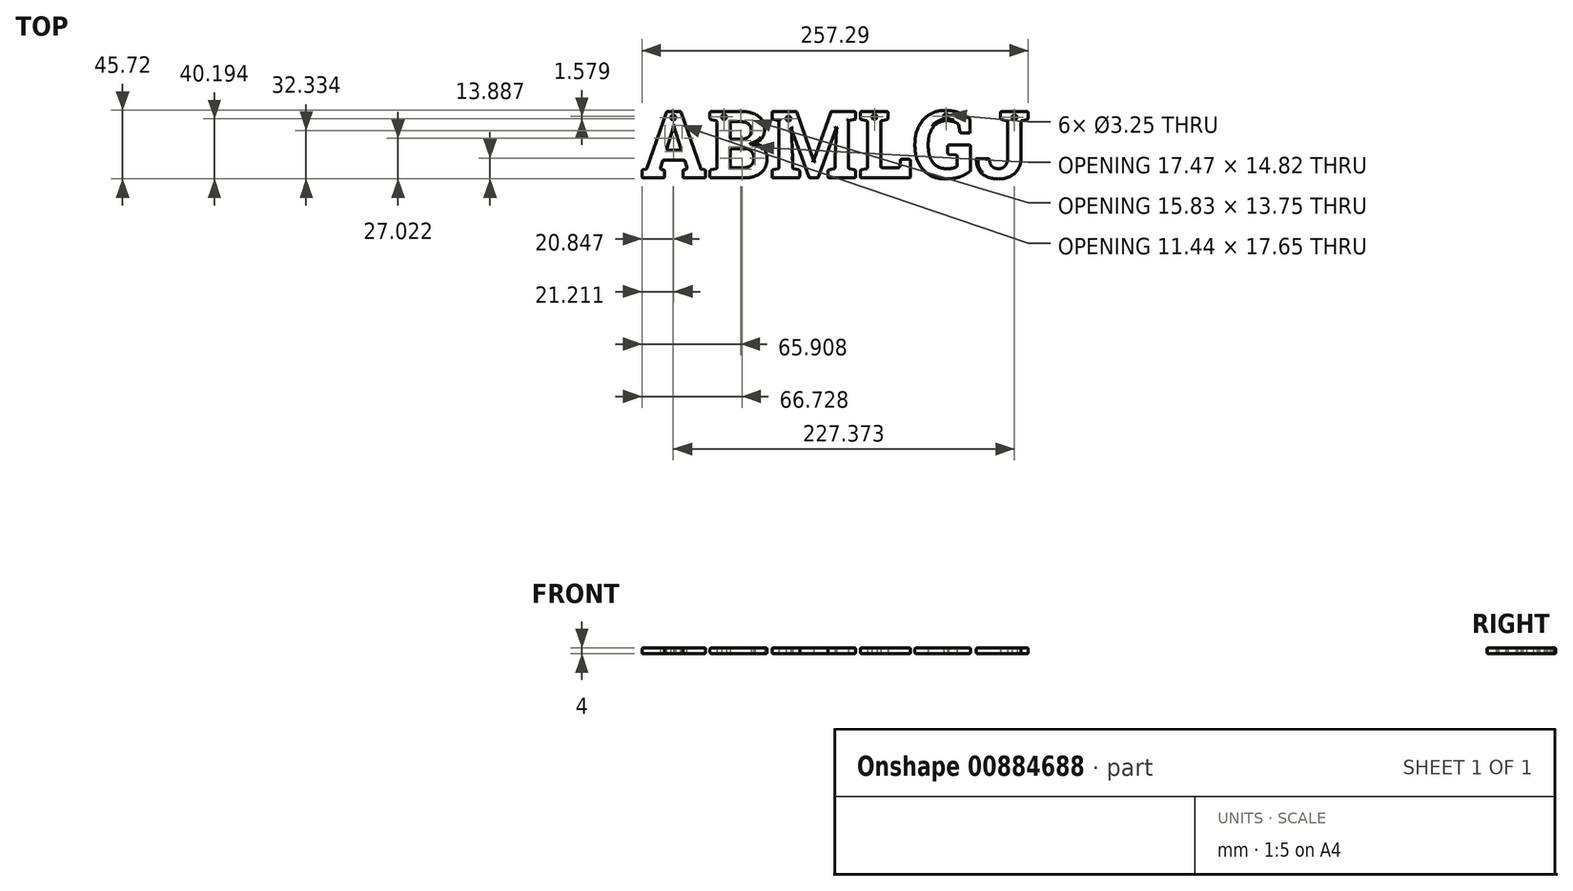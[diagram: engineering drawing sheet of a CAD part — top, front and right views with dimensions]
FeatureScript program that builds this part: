
annotation { "Feature Type Name" : "Feature", "Feature Type Description" : "" }
export const myFeature = defineFeature(function(context is Context, id is Id, definition is map)
    precondition{}
    {
        {
            var Q0;
            Q0=qCreatedBy(makeId("Top.planeOp"),FACE);
            var sketch = newSketch(context, id + "F0", { "sketchPlane" : qUnion([Q0])});
            skText(sketch, "E0", { "text": "ABMLGJ", "fontName": "RobotoSlab-Bold.ttf"});
            skCircle(sketch, "E1", {"center": v(-18.26, 12.84) * mm, "radius": 1.63 * mm});
            skCircle(sketch, "E2", {"center": v(15.58, 13.2) * mm, "radius": 1.63 * mm});
            skCircle(sketch, "E3", {"center": v(58.54, 12.08) * mm, "radius": 1.63 * mm});
            skCircle(sketch, "E4", {"center": v(115.8, 13.22) * mm, "radius": 1.63 * mm});
            skCircle(sketch, "E5", {"center": v(163.46, 13.66) * mm, "radius": 1.63 * mm});
            skCircle(sketch, "E6", {"center": v(209.1, 12.89) * mm, "radius": 1.63 * mm});
            const initialGuessF0  = {"E0": [-0.04036, -0.02747, 1, 0, 0.045]};
            skSetInitialGuess(sketch, initialGuessF0);
            skSolve(sketch);
        }
        {
            var Q0;
            Q0 = qSketchRegion(id + "F0", true);
            extrude(context, id + "F1", {"entities" : qUnion([Q0]), "depth" : 4 * mm, "offsetDistance" : 25 * mm});
        }
        {
            var Q0;
            Q0=makeQuery(id+"F1.opExtrude","CAP_FACE",FACE,{"disambiguationData":[OSD([sQuery(id+"F0.wireOp",EDGE,"E0.sketch_text.stroke-20"),sQuery(id+"F0.wireOp",EDGE,"E0.sketch_text.stroke-21"),sQuery(id+"F0.wireOp",EDGE,"E0.sketch_text.stroke-22"),sQuery(id+"F0.wireOp",EDGE,"E0.sketch_text.stroke-23"),sQuery(id+"F0.wireOp",EDGE,"E0.sketch_text.stroke-24"),sQuery(id+"F0.wireOp",EDGE,"E0.sketch_text.stroke-25"),sQuery(id+"F0.wireOp",EDGE,"E0.sketch_text.stroke-26"),sQuery(id+"F0.wireOp",EDGE,"E0.sketch_text.stroke-27"),sQuery(id+"F0.wireOp",EDGE,"E0.sketch_text.stroke-28"),sQuery(id+"F0.wireOp",EDGE,"E0.sketch_text.stroke-29"),sQuery(id+"F0.wireOp",EDGE,"E0.sketch_text.stroke-30"),sQuery(id+"F0.wireOp",EDGE,"E0.sketch_text.stroke-31"),sQuery(id+"F0.wireOp",EDGE,"E0.sketch_text.stroke-32"),sQuery(id+"F0.wireOp",EDGE,"E0.sketch_text.stroke-33"),sQuery(id+"F0.wireOp",EDGE,"E0.sketch_text.stroke-34"),sQuery(id+"F0.wireOp",EDGE,"E0.sketch_text.stroke-35"),sQuery(id+"F0.wireOp",EDGE,"E0.sketch_text.stroke-36"),sQuery(id+"F0.wireOp",EDGE,"E0.sketch_text.stroke-37"),sQuery(id+"F0.wireOp",EDGE,"E0.sketch_text.stroke-38"),sQuery(id+"F0.wireOp",EDGE,"E0.sketch_text.stroke-39"),sQuery(id+"F0.wireOp",EDGE,"E0.sketch_text.stroke-40"),sQuery(id+"F0.wireOp",EDGE,"E0.sketch_text.stroke-41"),sQuery(id+"F0.wireOp",EDGE,"E0.sketch_text.stroke-42"),sQuery(id+"F0.wireOp",EDGE,"E0.sketch_text.stroke-43"),sQuery(id+"F0.wireOp",EDGE,"E0.sketch_text.stroke-44"),sQuery(id+"F0.wireOp",EDGE,"E0.sketch_text.stroke-45"),sQuery(id+"F0.wireOp",EDGE,"E0.sketch_text.stroke-46"),sQuery(id+"F0.wireOp",EDGE,"E0.sketch_text.stroke-47"),sQuery(id+"F0.wireOp",EDGE,"E0.sketch_text.stroke-48"),sQuery(id+"F0.wireOp",EDGE,"E0.sketch_text.stroke-49"),sQuery(id+"F0.wireOp",EDGE,"E2")])],"isStart":false});
            var Q1;
            Q1=makeQuery(id+"F1.opExtrude","CAP_FACE",FACE,{"disambiguationData":[OSD([sQuery(id+"F0.wireOp",EDGE,"E0.sketch_text.stroke-50"),sQuery(id+"F0.wireOp",EDGE,"E0.sketch_text.stroke-51"),sQuery(id+"F0.wireOp",EDGE,"E0.sketch_text.stroke-52"),sQuery(id+"F0.wireOp",EDGE,"E0.sketch_text.stroke-53"),sQuery(id+"F0.wireOp",EDGE,"E0.sketch_text.stroke-54"),sQuery(id+"F0.wireOp",EDGE,"E0.sketch_text.stroke-55"),sQuery(id+"F0.wireOp",EDGE,"E0.sketch_text.stroke-56"),sQuery(id+"F0.wireOp",EDGE,"E0.sketch_text.stroke-57"),sQuery(id+"F0.wireOp",EDGE,"E0.sketch_text.stroke-58"),sQuery(id+"F0.wireOp",EDGE,"E0.sketch_text.stroke-59"),sQuery(id+"F0.wireOp",EDGE,"E0.sketch_text.stroke-60"),sQuery(id+"F0.wireOp",EDGE,"E0.sketch_text.stroke-61"),sQuery(id+"F0.wireOp",EDGE,"E0.sketch_text.stroke-62"),sQuery(id+"F0.wireOp",EDGE,"E0.sketch_text.stroke-63"),sQuery(id+"F0.wireOp",EDGE,"E0.sketch_text.stroke-64"),sQuery(id+"F0.wireOp",EDGE,"E0.sketch_text.stroke-65"),sQuery(id+"F0.wireOp",EDGE,"E0.sketch_text.stroke-66"),sQuery(id+"F0.wireOp",EDGE,"E0.sketch_text.stroke-67"),sQuery(id+"F0.wireOp",EDGE,"E0.sketch_text.stroke-68"),sQuery(id+"F0.wireOp",EDGE,"E0.sketch_text.stroke-69"),sQuery(id+"F0.wireOp",EDGE,"E0.sketch_text.stroke-70"),sQuery(id+"F0.wireOp",EDGE,"E0.sketch_text.stroke-71"),sQuery(id+"F0.wireOp",EDGE,"E0.sketch_text.stroke-72"),sQuery(id+"F0.wireOp",EDGE,"E0.sketch_text.stroke-73"),sQuery(id+"F0.wireOp",EDGE,"E0.sketch_text.stroke-74"),sQuery(id+"F0.wireOp",EDGE,"E0.sketch_text.stroke-75"),sQuery(id+"F0.wireOp",EDGE,"E0.sketch_text.stroke-76"),sQuery(id+"F0.wireOp",EDGE,"E0.sketch_text.stroke-77"),sQuery(id+"F0.wireOp",EDGE,"E0.sketch_text.stroke-78"),sQuery(id+"F0.wireOp",EDGE,"E0.sketch_text.stroke-79"),sQuery(id+"F0.wireOp",EDGE,"E0.sketch_text.stroke-80"),sQuery(id+"F0.wireOp",EDGE,"E3")])],"isStart":false});
            var Q2;
            Q2=makeQuery(id+"F1.opExtrude","CAP_FACE",FACE,{"disambiguationData":[OSD([sQuery(id+"F0.wireOp",EDGE,"E0.sketch_text.stroke-81"),sQuery(id+"F0.wireOp",EDGE,"E0.sketch_text.stroke-82"),sQuery(id+"F0.wireOp",EDGE,"E0.sketch_text.stroke-83"),sQuery(id+"F0.wireOp",EDGE,"E0.sketch_text.stroke-84"),sQuery(id+"F0.wireOp",EDGE,"E0.sketch_text.stroke-85"),sQuery(id+"F0.wireOp",EDGE,"E0.sketch_text.stroke-86"),sQuery(id+"F0.wireOp",EDGE,"E0.sketch_text.stroke-87"),sQuery(id+"F0.wireOp",EDGE,"E0.sketch_text.stroke-88"),sQuery(id+"F0.wireOp",EDGE,"E0.sketch_text.stroke-89"),sQuery(id+"F0.wireOp",EDGE,"E0.sketch_text.stroke-90"),sQuery(id+"F0.wireOp",EDGE,"E0.sketch_text.stroke-91"),sQuery(id+"F0.wireOp",EDGE,"E0.sketch_text.stroke-92"),sQuery(id+"F0.wireOp",EDGE,"E0.sketch_text.stroke-93"),sQuery(id+"F0.wireOp",EDGE,"E0.sketch_text.stroke-94"),sQuery(id+"F0.wireOp",EDGE,"E0.sketch_text.stroke-95"),sQuery(id+"F0.wireOp",EDGE,"E0.sketch_text.stroke-96"),sQuery(id+"F0.wireOp",EDGE,"E4")])],"isStart":false});
            var Q3;
            Q3=makeQuery(id+"F1.opExtrude","CAP_FACE",FACE,{"disambiguationData":[OSD([sQuery(id+"F0.wireOp",EDGE,"E0.sketch_text.stroke-97"),sQuery(id+"F0.wireOp",EDGE,"E0.sketch_text.stroke-98"),sQuery(id+"F0.wireOp",EDGE,"E0.sketch_text.stroke-99"),sQuery(id+"F0.wireOp",EDGE,"E0.sketch_text.stroke-100"),sQuery(id+"F0.wireOp",EDGE,"E0.sketch_text.stroke-101"),sQuery(id+"F0.wireOp",EDGE,"E0.sketch_text.stroke-102"),sQuery(id+"F0.wireOp",EDGE,"E0.sketch_text.stroke-103"),sQuery(id+"F0.wireOp",EDGE,"E0.sketch_text.stroke-104"),sQuery(id+"F0.wireOp",EDGE,"E0.sketch_text.stroke-105"),sQuery(id+"F0.wireOp",EDGE,"E0.sketch_text.stroke-106"),sQuery(id+"F0.wireOp",EDGE,"E0.sketch_text.stroke-107"),sQuery(id+"F0.wireOp",EDGE,"E0.sketch_text.stroke-108"),sQuery(id+"F0.wireOp",EDGE,"E0.sketch_text.stroke-109"),sQuery(id+"F0.wireOp",EDGE,"E0.sketch_text.stroke-110"),sQuery(id+"F0.wireOp",EDGE,"E0.sketch_text.stroke-111"),sQuery(id+"F0.wireOp",EDGE,"E0.sketch_text.stroke-112"),sQuery(id+"F0.wireOp",EDGE,"E0.sketch_text.stroke-113"),sQuery(id+"F0.wireOp",EDGE,"E0.sketch_text.stroke-114"),sQuery(id+"F0.wireOp",EDGE,"E0.sketch_text.stroke-115"),sQuery(id+"F0.wireOp",EDGE,"E0.sketch_text.stroke-116"),sQuery(id+"F0.wireOp",EDGE,"E0.sketch_text.stroke-117"),sQuery(id+"F0.wireOp",EDGE,"E0.sketch_text.stroke-118"),sQuery(id+"F0.wireOp",EDGE,"E0.sketch_text.stroke-119"),sQuery(id+"F0.wireOp",EDGE,"E0.sketch_text.stroke-120"),sQuery(id+"F0.wireOp",EDGE,"E0.sketch_text.stroke-121"),sQuery(id+"F0.wireOp",EDGE,"E0.sketch_text.stroke-122"),sQuery(id+"F0.wireOp",EDGE,"E5")])],"isStart":false});
            var Q4;
            Q4=makeQuery(id+"F1.opExtrude","CAP_FACE",FACE,{"disambiguationData":[OSD([sQuery(id+"F0.wireOp",EDGE,"E0.sketch_text.stroke-123"),sQuery(id+"F0.wireOp",EDGE,"E0.sketch_text.stroke-124"),sQuery(id+"F0.wireOp",EDGE,"E0.sketch_text.stroke-125"),sQuery(id+"F0.wireOp",EDGE,"E0.sketch_text.stroke-126"),sQuery(id+"F0.wireOp",EDGE,"E0.sketch_text.stroke-127"),sQuery(id+"F0.wireOp",EDGE,"E0.sketch_text.stroke-128"),sQuery(id+"F0.wireOp",EDGE,"E0.sketch_text.stroke-129"),sQuery(id+"F0.wireOp",EDGE,"E0.sketch_text.stroke-130"),sQuery(id+"F0.wireOp",EDGE,"E0.sketch_text.stroke-131"),sQuery(id+"F0.wireOp",EDGE,"E0.sketch_text.stroke-132"),sQuery(id+"F0.wireOp",EDGE,"E0.sketch_text.stroke-133"),sQuery(id+"F0.wireOp",EDGE,"E0.sketch_text.stroke-134"),sQuery(id+"F0.wireOp",EDGE,"E0.sketch_text.stroke-135"),sQuery(id+"F0.wireOp",EDGE,"E0.sketch_text.stroke-136"),sQuery(id+"F0.wireOp",EDGE,"E0.sketch_text.stroke-137"),sQuery(id+"F0.wireOp",EDGE,"E0.sketch_text.stroke-138"),sQuery(id+"F0.wireOp",EDGE,"E0.sketch_text.stroke-139"),sQuery(id+"F0.wireOp",EDGE,"E0.sketch_text.stroke-140"),sQuery(id+"F0.wireOp",EDGE,"E6")])],"isStart":false});
            var Q5;
            Q5=makeQuery(id+"F1.opExtrude","CAP_FACE",FACE,{"disambiguationData":[OSD([sQuery(id+"F0.wireOp",EDGE,"E0.sketch_text.stroke-123"),sQuery(id+"F0.wireOp",EDGE,"E0.sketch_text.stroke-124"),sQuery(id+"F0.wireOp",EDGE,"E0.sketch_text.stroke-125"),sQuery(id+"F0.wireOp",EDGE,"E0.sketch_text.stroke-126"),sQuery(id+"F0.wireOp",EDGE,"E0.sketch_text.stroke-127"),sQuery(id+"F0.wireOp",EDGE,"E0.sketch_text.stroke-128"),sQuery(id+"F0.wireOp",EDGE,"E0.sketch_text.stroke-129"),sQuery(id+"F0.wireOp",EDGE,"E0.sketch_text.stroke-130"),sQuery(id+"F0.wireOp",EDGE,"E0.sketch_text.stroke-131"),sQuery(id+"F0.wireOp",EDGE,"E0.sketch_text.stroke-132"),sQuery(id+"F0.wireOp",EDGE,"E0.sketch_text.stroke-133"),sQuery(id+"F0.wireOp",EDGE,"E0.sketch_text.stroke-134"),sQuery(id+"F0.wireOp",EDGE,"E0.sketch_text.stroke-135"),sQuery(id+"F0.wireOp",EDGE,"E0.sketch_text.stroke-136"),sQuery(id+"F0.wireOp",EDGE,"E0.sketch_text.stroke-137"),sQuery(id+"F0.wireOp",EDGE,"E0.sketch_text.stroke-138"),sQuery(id+"F0.wireOp",EDGE,"E0.sketch_text.stroke-139"),sQuery(id+"F0.wireOp",EDGE,"E0.sketch_text.stroke-140"),sQuery(id+"F0.wireOp",EDGE,"E6")])],"isStart":true});
            var Q6;
            Q6=makeQuery(id+"F1.opExtrude","CAP_FACE",FACE,{"disambiguationData":[OSD([sQuery(id+"F0.wireOp",EDGE,"E0.sketch_text.stroke-97"),sQuery(id+"F0.wireOp",EDGE,"E0.sketch_text.stroke-98"),sQuery(id+"F0.wireOp",EDGE,"E0.sketch_text.stroke-99"),sQuery(id+"F0.wireOp",EDGE,"E0.sketch_text.stroke-100"),sQuery(id+"F0.wireOp",EDGE,"E0.sketch_text.stroke-101"),sQuery(id+"F0.wireOp",EDGE,"E0.sketch_text.stroke-102"),sQuery(id+"F0.wireOp",EDGE,"E0.sketch_text.stroke-103"),sQuery(id+"F0.wireOp",EDGE,"E0.sketch_text.stroke-104"),sQuery(id+"F0.wireOp",EDGE,"E0.sketch_text.stroke-105"),sQuery(id+"F0.wireOp",EDGE,"E0.sketch_text.stroke-106"),sQuery(id+"F0.wireOp",EDGE,"E0.sketch_text.stroke-107"),sQuery(id+"F0.wireOp",EDGE,"E0.sketch_text.stroke-108"),sQuery(id+"F0.wireOp",EDGE,"E0.sketch_text.stroke-109"),sQuery(id+"F0.wireOp",EDGE,"E0.sketch_text.stroke-110"),sQuery(id+"F0.wireOp",EDGE,"E0.sketch_text.stroke-111"),sQuery(id+"F0.wireOp",EDGE,"E0.sketch_text.stroke-112"),sQuery(id+"F0.wireOp",EDGE,"E0.sketch_text.stroke-113"),sQuery(id+"F0.wireOp",EDGE,"E0.sketch_text.stroke-114"),sQuery(id+"F0.wireOp",EDGE,"E0.sketch_text.stroke-115"),sQuery(id+"F0.wireOp",EDGE,"E0.sketch_text.stroke-116"),sQuery(id+"F0.wireOp",EDGE,"E0.sketch_text.stroke-117"),sQuery(id+"F0.wireOp",EDGE,"E0.sketch_text.stroke-118"),sQuery(id+"F0.wireOp",EDGE,"E0.sketch_text.stroke-119"),sQuery(id+"F0.wireOp",EDGE,"E0.sketch_text.stroke-120"),sQuery(id+"F0.wireOp",EDGE,"E0.sketch_text.stroke-121"),sQuery(id+"F0.wireOp",EDGE,"E0.sketch_text.stroke-122"),sQuery(id+"F0.wireOp",EDGE,"E5")])],"isStart":true});
            var Q7;
            Q7=makeQuery(id+"F1.opExtrude","CAP_FACE",FACE,{"disambiguationData":[OSD([sQuery(id+"F0.wireOp",EDGE,"E0.sketch_text.stroke-81"),sQuery(id+"F0.wireOp",EDGE,"E0.sketch_text.stroke-82"),sQuery(id+"F0.wireOp",EDGE,"E0.sketch_text.stroke-83"),sQuery(id+"F0.wireOp",EDGE,"E0.sketch_text.stroke-84"),sQuery(id+"F0.wireOp",EDGE,"E0.sketch_text.stroke-85"),sQuery(id+"F0.wireOp",EDGE,"E0.sketch_text.stroke-86"),sQuery(id+"F0.wireOp",EDGE,"E0.sketch_text.stroke-87"),sQuery(id+"F0.wireOp",EDGE,"E0.sketch_text.stroke-88"),sQuery(id+"F0.wireOp",EDGE,"E0.sketch_text.stroke-89"),sQuery(id+"F0.wireOp",EDGE,"E0.sketch_text.stroke-90"),sQuery(id+"F0.wireOp",EDGE,"E0.sketch_text.stroke-91"),sQuery(id+"F0.wireOp",EDGE,"E0.sketch_text.stroke-92"),sQuery(id+"F0.wireOp",EDGE,"E0.sketch_text.stroke-93"),sQuery(id+"F0.wireOp",EDGE,"E0.sketch_text.stroke-94"),sQuery(id+"F0.wireOp",EDGE,"E0.sketch_text.stroke-95"),sQuery(id+"F0.wireOp",EDGE,"E0.sketch_text.stroke-96"),sQuery(id+"F0.wireOp",EDGE,"E4")])],"isStart":true});
            var Q8;
            Q8=makeQuery(id+"F1.opExtrude","CAP_FACE",FACE,{"disambiguationData":[OSD([sQuery(id+"F0.wireOp",EDGE,"E0.sketch_text.stroke-50"),sQuery(id+"F0.wireOp",EDGE,"E0.sketch_text.stroke-51"),sQuery(id+"F0.wireOp",EDGE,"E0.sketch_text.stroke-52"),sQuery(id+"F0.wireOp",EDGE,"E0.sketch_text.stroke-53"),sQuery(id+"F0.wireOp",EDGE,"E0.sketch_text.stroke-54"),sQuery(id+"F0.wireOp",EDGE,"E0.sketch_text.stroke-55"),sQuery(id+"F0.wireOp",EDGE,"E0.sketch_text.stroke-56"),sQuery(id+"F0.wireOp",EDGE,"E0.sketch_text.stroke-57"),sQuery(id+"F0.wireOp",EDGE,"E0.sketch_text.stroke-58"),sQuery(id+"F0.wireOp",EDGE,"E0.sketch_text.stroke-59"),sQuery(id+"F0.wireOp",EDGE,"E0.sketch_text.stroke-60"),sQuery(id+"F0.wireOp",EDGE,"E0.sketch_text.stroke-61"),sQuery(id+"F0.wireOp",EDGE,"E0.sketch_text.stroke-62"),sQuery(id+"F0.wireOp",EDGE,"E0.sketch_text.stroke-63"),sQuery(id+"F0.wireOp",EDGE,"E0.sketch_text.stroke-64"),sQuery(id+"F0.wireOp",EDGE,"E0.sketch_text.stroke-65"),sQuery(id+"F0.wireOp",EDGE,"E0.sketch_text.stroke-66"),sQuery(id+"F0.wireOp",EDGE,"E0.sketch_text.stroke-67"),sQuery(id+"F0.wireOp",EDGE,"E0.sketch_text.stroke-68"),sQuery(id+"F0.wireOp",EDGE,"E0.sketch_text.stroke-69"),sQuery(id+"F0.wireOp",EDGE,"E0.sketch_text.stroke-70"),sQuery(id+"F0.wireOp",EDGE,"E0.sketch_text.stroke-71"),sQuery(id+"F0.wireOp",EDGE,"E0.sketch_text.stroke-72"),sQuery(id+"F0.wireOp",EDGE,"E0.sketch_text.stroke-73"),sQuery(id+"F0.wireOp",EDGE,"E0.sketch_text.stroke-74"),sQuery(id+"F0.wireOp",EDGE,"E0.sketch_text.stroke-75"),sQuery(id+"F0.wireOp",EDGE,"E0.sketch_text.stroke-76"),sQuery(id+"F0.wireOp",EDGE,"E0.sketch_text.stroke-77"),sQuery(id+"F0.wireOp",EDGE,"E0.sketch_text.stroke-78"),sQuery(id+"F0.wireOp",EDGE,"E0.sketch_text.stroke-79"),sQuery(id+"F0.wireOp",EDGE,"E0.sketch_text.stroke-80"),sQuery(id+"F0.wireOp",EDGE,"E3")])],"isStart":true});
            var Q9;
            Q9=makeQuery(id+"F1.opExtrude","CAP_FACE",FACE,{"disambiguationData":[OSD([sQuery(id+"F0.wireOp",EDGE,"E0.sketch_text.stroke-20"),sQuery(id+"F0.wireOp",EDGE,"E0.sketch_text.stroke-21"),sQuery(id+"F0.wireOp",EDGE,"E0.sketch_text.stroke-22"),sQuery(id+"F0.wireOp",EDGE,"E0.sketch_text.stroke-23"),sQuery(id+"F0.wireOp",EDGE,"E0.sketch_text.stroke-24"),sQuery(id+"F0.wireOp",EDGE,"E0.sketch_text.stroke-25"),sQuery(id+"F0.wireOp",EDGE,"E0.sketch_text.stroke-26"),sQuery(id+"F0.wireOp",EDGE,"E0.sketch_text.stroke-27"),sQuery(id+"F0.wireOp",EDGE,"E0.sketch_text.stroke-28"),sQuery(id+"F0.wireOp",EDGE,"E0.sketch_text.stroke-29"),sQuery(id+"F0.wireOp",EDGE,"E0.sketch_text.stroke-30"),sQuery(id+"F0.wireOp",EDGE,"E0.sketch_text.stroke-31"),sQuery(id+"F0.wireOp",EDGE,"E0.sketch_text.stroke-32"),sQuery(id+"F0.wireOp",EDGE,"E0.sketch_text.stroke-33"),sQuery(id+"F0.wireOp",EDGE,"E0.sketch_text.stroke-34"),sQuery(id+"F0.wireOp",EDGE,"E0.sketch_text.stroke-35"),sQuery(id+"F0.wireOp",EDGE,"E0.sketch_text.stroke-36"),sQuery(id+"F0.wireOp",EDGE,"E0.sketch_text.stroke-37"),sQuery(id+"F0.wireOp",EDGE,"E0.sketch_text.stroke-38"),sQuery(id+"F0.wireOp",EDGE,"E0.sketch_text.stroke-39"),sQuery(id+"F0.wireOp",EDGE,"E0.sketch_text.stroke-40"),sQuery(id+"F0.wireOp",EDGE,"E0.sketch_text.stroke-41"),sQuery(id+"F0.wireOp",EDGE,"E0.sketch_text.stroke-42"),sQuery(id+"F0.wireOp",EDGE,"E0.sketch_text.stroke-43"),sQuery(id+"F0.wireOp",EDGE,"E0.sketch_text.stroke-44"),sQuery(id+"F0.wireOp",EDGE,"E0.sketch_text.stroke-45"),sQuery(id+"F0.wireOp",EDGE,"E0.sketch_text.stroke-46"),sQuery(id+"F0.wireOp",EDGE,"E0.sketch_text.stroke-47"),sQuery(id+"F0.wireOp",EDGE,"E0.sketch_text.stroke-48"),sQuery(id+"F0.wireOp",EDGE,"E0.sketch_text.stroke-49"),sQuery(id+"F0.wireOp",EDGE,"E2")])],"isStart":true});
            var Q10;
            Q10=makeQuery(id+"F1.opExtrude","CAP_FACE",FACE,{"disambiguationData":[OSD([sQuery(id+"F0.wireOp",EDGE,"E0.sketch_text.stroke-0"),sQuery(id+"F0.wireOp",EDGE,"E0.sketch_text.stroke-1"),sQuery(id+"F0.wireOp",EDGE,"E0.sketch_text.stroke-2"),sQuery(id+"F0.wireOp",EDGE,"E0.sketch_text.stroke-3"),sQuery(id+"F0.wireOp",EDGE,"E0.sketch_text.stroke-4"),sQuery(id+"F0.wireOp",EDGE,"E0.sketch_text.stroke-5"),sQuery(id+"F0.wireOp",EDGE,"E0.sketch_text.stroke-6"),sQuery(id+"F0.wireOp",EDGE,"E0.sketch_text.stroke-7"),sQuery(id+"F0.wireOp",EDGE,"E0.sketch_text.stroke-8"),sQuery(id+"F0.wireOp",EDGE,"E0.sketch_text.stroke-9"),sQuery(id+"F0.wireOp",EDGE,"E0.sketch_text.stroke-10"),sQuery(id+"F0.wireOp",EDGE,"E0.sketch_text.stroke-11"),sQuery(id+"F0.wireOp",EDGE,"E0.sketch_text.stroke-12"),sQuery(id+"F0.wireOp",EDGE,"E0.sketch_text.stroke-13"),sQuery(id+"F0.wireOp",EDGE,"E0.sketch_text.stroke-14"),sQuery(id+"F0.wireOp",EDGE,"E0.sketch_text.stroke-15"),sQuery(id+"F0.wireOp",EDGE,"E0.sketch_text.stroke-16"),sQuery(id+"F0.wireOp",EDGE,"E0.sketch_text.stroke-17"),sQuery(id+"F0.wireOp",EDGE,"E0.sketch_text.stroke-18"),sQuery(id+"F0.wireOp",EDGE,"E0.sketch_text.stroke-19"),sQuery(id+"F0.wireOp",EDGE,"E1")])],"isStart":true});
            var Q11;
            Q11=makeQuery(id+"F1.opExtrude","SWEPT_FACE",FACE,{"disambiguationData":[OSD([sQuery(id+"F0.wireOp",EDGE,"E0.sketch_text.stroke-15")])]});
            var Q12;
            Q12=makeQuery(id+"F1.opExtrude","SWEPT_FACE",FACE,{"disambiguationData":[OSD([sQuery(id+"F0.wireOp",EDGE,"E0.sketch_text.stroke-14")])]});
            var Q13;
            Q13=makeQuery(id+"F1.opExtrude","SWEPT_FACE",FACE,{"disambiguationData":[OSD([sQuery(id+"F0.wireOp",EDGE,"E0.sketch_text.stroke-6")])]});
            var Q14;
            Q14=makeQuery(id+"F1.opExtrude","SWEPT_FACE",FACE,{"disambiguationData":[OSD([sQuery(id+"F0.wireOp",EDGE,"E0.sketch_text.stroke-1")])]});
            var Q15;
            Q15=makeQuery(id+"F1.opExtrude","SWEPT_FACE",FACE,{"disambiguationData":[OSD([sQuery(id+"F0.wireOp",EDGE,"E0.sketch_text.stroke-10")])]});
            var Q16;
            Q16=makeQuery(id+"F1.opExtrude","SWEPT_FACE",FACE,{"disambiguationData":[OSD([sQuery(id+"F0.wireOp",EDGE,"E0.sketch_text.stroke-7")])]});
            var Q17;
            Q17=makeQuery(id+"F1.opExtrude","SWEPT_FACE",FACE,{"disambiguationData":[OSD([sQuery(id+"F0.wireOp",EDGE,"E0.sketch_text.stroke-13")])]});
            var Q18;
            Q18=makeQuery(id+"F1.opExtrude","SWEPT_FACE",FACE,{"disambiguationData":[OSD([sQuery(id+"F0.wireOp",EDGE,"E0.sketch_text.stroke-5")])]});
            var Q19;
            Q19=makeQuery(id+"F1.opExtrude","SWEPT_FACE",FACE,{"disambiguationData":[OSD([sQuery(id+"F0.wireOp",EDGE,"E0.sketch_text.stroke-3")])]});
            var Q20;
            Q20=makeQuery(id+"F1.opExtrude","CAP_FACE",FACE,{"disambiguationData":[OSD([sQuery(id+"F0.wireOp",EDGE,"E0.sketch_text.stroke-0"),sQuery(id+"F0.wireOp",EDGE,"E0.sketch_text.stroke-1"),sQuery(id+"F0.wireOp",EDGE,"E0.sketch_text.stroke-2"),sQuery(id+"F0.wireOp",EDGE,"E0.sketch_text.stroke-3"),sQuery(id+"F0.wireOp",EDGE,"E0.sketch_text.stroke-4"),sQuery(id+"F0.wireOp",EDGE,"E0.sketch_text.stroke-5"),sQuery(id+"F0.wireOp",EDGE,"E0.sketch_text.stroke-6"),sQuery(id+"F0.wireOp",EDGE,"E0.sketch_text.stroke-7"),sQuery(id+"F0.wireOp",EDGE,"E0.sketch_text.stroke-8"),sQuery(id+"F0.wireOp",EDGE,"E0.sketch_text.stroke-9"),sQuery(id+"F0.wireOp",EDGE,"E0.sketch_text.stroke-10"),sQuery(id+"F0.wireOp",EDGE,"E0.sketch_text.stroke-11"),sQuery(id+"F0.wireOp",EDGE,"E0.sketch_text.stroke-12"),sQuery(id+"F0.wireOp",EDGE,"E0.sketch_text.stroke-13"),sQuery(id+"F0.wireOp",EDGE,"E0.sketch_text.stroke-14"),sQuery(id+"F0.wireOp",EDGE,"E0.sketch_text.stroke-15"),sQuery(id+"F0.wireOp",EDGE,"E0.sketch_text.stroke-16"),sQuery(id+"F0.wireOp",EDGE,"E0.sketch_text.stroke-17"),sQuery(id+"F0.wireOp",EDGE,"E0.sketch_text.stroke-18"),sQuery(id+"F0.wireOp",EDGE,"E0.sketch_text.stroke-19"),sQuery(id+"F0.wireOp",EDGE,"E1")])],"isStart":false});
            var Q21;
            Q21=makeQuery(id+"F1.opExtrude","SWEPT_FACE",FACE,{"disambiguationData":[OSD([sQuery(id+"F0.wireOp",EDGE,"E0.sketch_text.stroke-33")])]});
            var Q22;
            Q22=makeQuery(id+"F1.opExtrude","SWEPT_FACE",FACE,{"disambiguationData":[OSD([sQuery(id+"F0.wireOp",EDGE,"E0.sketch_text.stroke-29")])]});
            var Q23;
            Q23=makeQuery(id+"F1.opExtrude","SWEPT_EDGE",EDGE,{"disambiguationData":[OSD([sQuery(id+"F0.wireOp",EDGE,"E0.sketch_text.stroke-30"),sQuery(id+"F0.wireOp",EDGE,"E0.sketch_text.stroke-31")])]});
            var Q24;
            Q24=makeQuery(id+"F1.opExtrude","SWEPT_EDGE",EDGE,{"disambiguationData":[OSD([sQuery(id+"F0.wireOp",EDGE,"E0.sketch_text.stroke-31"),sQuery(id+"F0.wireOp",EDGE,"E0.sketch_text.stroke-32")])]});
            var Q25;
            Q25=makeQuery(id+"F1.opExtrude","SWEPT_EDGE",EDGE,{"disambiguationData":[OSD([sQuery(id+"F0.wireOp",EDGE,"E0.sketch_text.stroke-16"),sQuery(id+"F0.wireOp",EDGE,"E0.sketch_text.stroke-17")])]});
            var Q26;
            Q26=makeQuery(id+"F1.opExtrude","SWEPT_EDGE",EDGE,{"disambiguationData":[OSD([sQuery(id+"F0.wireOp",EDGE,"E0.sketch_text.stroke-16"),sQuery(id+"F0.wireOp",EDGE,"E0.sketch_text.stroke-19")])]});
            var Q27;
            Q27=makeQuery(id+"F1.opExtrude","SWEPT_EDGE",EDGE,{"disambiguationData":[OSD([sQuery(id+"F0.wireOp",EDGE,"E0.sketch_text.stroke-11"),sQuery(id+"F0.wireOp",EDGE,"E0.sketch_text.stroke-12")])]});
            var Q28;
            Q28=makeQuery(id+"F1.opExtrude","SWEPT_EDGE",EDGE,{"disambiguationData":[OSD([sQuery(id+"F0.wireOp",EDGE,"E0.sketch_text.stroke-8"),sQuery(id+"F0.wireOp",EDGE,"E0.sketch_text.stroke-9")])]});
            var Q29;
            Q29=makeQuery(id+"F1.opExtrude","SWEPT_EDGE",EDGE,{"disambiguationData":[OSD([sQuery(id+"F0.wireOp",EDGE,"E0.sketch_text.stroke-36"),sQuery(id+"F0.wireOp",EDGE,"E0.sketch_text.stroke-37")])]});
            var Q30;
            Q30=makeQuery(id+"F1.opExtrude","SWEPT_EDGE",EDGE,{"disambiguationData":[OSD([sQuery(id+"F0.wireOp",EDGE,"E0.sketch_text.stroke-43"),sQuery(id+"F0.wireOp",EDGE,"E0.sketch_text.stroke-49")])]});
            var Q31;
            Q31=makeQuery(id+"F1.opExtrude","SWEPT_EDGE",EDGE,{"disambiguationData":[OSD([sQuery(id+"F0.wireOp",EDGE,"E0.sketch_text.stroke-48"),sQuery(id+"F0.wireOp",EDGE,"E0.sketch_text.stroke-49")])]});
            var Q32;
            Q32=makeQuery(id+"F1.opExtrude","SWEPT_EDGE",EDGE,{"disambiguationData":[OSD([sQuery(id+"F0.wireOp",EDGE,"E0.sketch_text.stroke-36"),sQuery(id+"F0.wireOp",EDGE,"E0.sketch_text.stroke-42")])]});
            var Q33;
            Q33=makeQuery(id+"F1.opExtrude","SWEPT_FACE",FACE,{"disambiguationData":[OSD([sQuery(id+"F0.wireOp",EDGE,"E0.sketch_text.stroke-58")])]});
            var Q34;
            Q34=makeQuery(id+"F1.opExtrude","SWEPT_FACE",FACE,{"disambiguationData":[OSD([sQuery(id+"F0.wireOp",EDGE,"E0.sketch_text.stroke-75")])]});
            var Q35;
            Q35=makeQuery(id+"F1.opExtrude","SWEPT_FACE",FACE,{"disambiguationData":[OSD([sQuery(id+"F0.wireOp",EDGE,"E0.sketch_text.stroke-65"),sQuery(id+"F0.wireOp",EDGE,"E0.sketch_text.stroke-66")])]});
            var Q36;
            Q36=makeQuery(id+"F1.opExtrude","SWEPT_FACE",FACE,{"disambiguationData":[OSD([sQuery(id+"F0.wireOp",EDGE,"E0.sketch_text.stroke-70")])]});
            var Q37;
            Q37=makeQuery(id+"F1.opExtrude","SWEPT_FACE",FACE,{"disambiguationData":[OSD([sQuery(id+"F0.wireOp",EDGE,"E0.sketch_text.stroke-86"),sQuery(id+"F0.wireOp",EDGE,"E0.sketch_text.stroke-87"),sQuery(id+"F0.wireOp",EDGE,"E0.sketch_text.stroke-88")])]});
            var Q38;
            Q38=makeQuery(id+"F1.opExtrude","SWEPT_FACE",FACE,{"disambiguationData":[OSD([sQuery(id+"F0.wireOp",EDGE,"E0.sketch_text.stroke-59")])]});
            var Q39;
            Q39=makeQuery(id+"F1.opExtrude","SWEPT_FACE",FACE,{"disambiguationData":[OSD([sQuery(id+"F0.wireOp",EDGE,"E0.sketch_text.stroke-76")])]});
            var Q40;
            Q40=makeQuery(id+"F1.opExtrude","SWEPT_FACE",FACE,{"disambiguationData":[OSD([sQuery(id+"F0.wireOp",EDGE,"E0.sketch_text.stroke-96")])]});
            var Q41;
            Q41=makeQuery(id+"F1.opExtrude","SWEPT_FACE",FACE,{"disambiguationData":[OSD([sQuery(id+"F0.wireOp",EDGE,"E0.sketch_text.stroke-84")])]});
            var Q42;
            Q42=makeQuery(id+"F1.opExtrude","SWEPT_FACE",FACE,{"disambiguationData":[OSD([sQuery(id+"F0.wireOp",EDGE,"E0.sketch_text.stroke-90")])]});
            var Q43;
            Q43=makeQuery(id+"F1.opExtrude","SWEPT_FACE",FACE,{"disambiguationData":[OSD([sQuery(id+"F0.wireOp",EDGE,"E0.sketch_text.stroke-52")])]});
            var Q44;
            Q44=makeQuery(id+"F1.opExtrude","SWEPT_EDGE",EDGE,{"disambiguationData":[OSD([sQuery(id+"F0.wireOp",EDGE,"E0.sketch_text.stroke-56"),sQuery(id+"F0.wireOp",EDGE,"E0.sketch_text.stroke-57")])]});
            var Q45;
            Q45=makeQuery(id+"F1.opExtrude","SWEPT_EDGE",EDGE,{"disambiguationData":[OSD([sQuery(id+"F0.wireOp",EDGE,"E0.sketch_text.stroke-73"),sQuery(id+"F0.wireOp",EDGE,"E0.sketch_text.stroke-74")])]});
            var Q46;
            Q46=makeQuery(id+"F1.opExtrude","SWEPT_EDGE",EDGE,{"disambiguationData":[OSD([sQuery(id+"F0.wireOp",EDGE,"E0.sketch_text.stroke-78"),sQuery(id+"F0.wireOp",EDGE,"E0.sketch_text.stroke-79")])]});
            var Q47;
            Q47=makeQuery(id+"F1.opExtrude","SWEPT_EDGE",EDGE,{"disambiguationData":[OSD([sQuery(id+"F0.wireOp",EDGE,"E0.sketch_text.stroke-61"),sQuery(id+"F0.wireOp",EDGE,"E0.sketch_text.stroke-62")])]});
            var Q48;
            Q48=makeQuery(id+"F1.opExtrude","SWEPT_EDGE",EDGE,{"disambiguationData":[OSD([sQuery(id+"F0.wireOp",EDGE,"E0.sketch_text.stroke-60"),sQuery(id+"F0.wireOp",EDGE,"E0.sketch_text.stroke-61")])]});
            var Q49;
            Q49=makeQuery(id+"F1.opExtrude","SWEPT_EDGE",EDGE,{"disambiguationData":[OSD([sQuery(id+"F0.wireOp",EDGE,"E0.sketch_text.stroke-81"),sQuery(id+"F0.wireOp",EDGE,"E0.sketch_text.stroke-82")])]});
            var Q50;
            Q50=makeQuery(id+"F1.opExtrude","SWEPT_EDGE",EDGE,{"disambiguationData":[OSD([sQuery(id+"F0.wireOp",EDGE,"E0.sketch_text.stroke-82"),sQuery(id+"F0.wireOp",EDGE,"E0.sketch_text.stroke-83")])]});
            var Q51;
            Q51=makeQuery(id+"F1.opExtrude","SWEPT_EDGE",EDGE,{"disambiguationData":[OSD([sQuery(id+"F0.wireOp",EDGE,"E0.sketch_text.stroke-92"),sQuery(id+"F0.wireOp",EDGE,"E0.sketch_text.stroke-93")])]});
            var Q52;
            Q52=makeQuery(id+"F1.opExtrude","SWEPT_EDGE",EDGE,{"disambiguationData":[OSD([sQuery(id+"F0.wireOp",EDGE,"E0.sketch_text.stroke-93"),sQuery(id+"F0.wireOp",EDGE,"E0.sketch_text.stroke-94")])]});
            var Q53;
            Q53=makeQuery(id+"F1.opExtrude","SWEPT_EDGE",EDGE,{"disambiguationData":[OSD([sQuery(id+"F0.wireOp",EDGE,"E0.sketch_text.stroke-94"),sQuery(id+"F0.wireOp",EDGE,"E0.sketch_text.stroke-95")])]});
            var Q54;
            Q54=makeQuery(id+"F1.opExtrude","SWEPT_EDGE",EDGE,{"disambiguationData":[OSD([sQuery(id+"F0.wireOp",EDGE,"E0.sketch_text.stroke-91"),sQuery(id+"F0.wireOp",EDGE,"E0.sketch_text.stroke-92")])]});
            var Q55;
            Q55=makeQuery(id+"F1.opExtrude","SWEPT_EDGE",EDGE,{"disambiguationData":[OSD([sQuery(id+"F0.wireOp",EDGE,"E0.sketch_text.stroke-105"),sQuery(id+"F0.wireOp",EDGE,"E0.sketch_text.stroke-106")])]});
            var Q56;
            Q56=makeQuery(id+"F1.opExtrude","SWEPT_EDGE",EDGE,{"disambiguationData":[OSD([sQuery(id+"F0.wireOp",EDGE,"E0.sketch_text.stroke-121"),sQuery(id+"F0.wireOp",EDGE,"E0.sketch_text.stroke-122")])]});
            var Q57;
            Q57=makeQuery(id+"F1.opExtrude","SWEPT_EDGE",EDGE,{"disambiguationData":[OSD([sQuery(id+"F0.wireOp",EDGE,"E0.sketch_text.stroke-97"),sQuery(id+"F0.wireOp",EDGE,"E0.sketch_text.stroke-122")])]});
            var Q58;
            Q58=makeQuery(id+"F1.opExtrude","SWEPT_EDGE",EDGE,{"disambiguationData":[OSD([sQuery(id+"F0.wireOp",EDGE,"E0.sketch_text.stroke-108"),sQuery(id+"F0.wireOp",EDGE,"E0.sketch_text.stroke-109")])]});
            var Q59;
            Q59=makeQuery(id+"F1.opExtrude","SWEPT_EDGE",EDGE,{"disambiguationData":[OSD([sQuery(id+"F0.wireOp",EDGE,"E0.sketch_text.stroke-107"),sQuery(id+"F0.wireOp",EDGE,"E0.sketch_text.stroke-108")])]});
            var Q60;
            Q60=makeQuery(id+"F1.opExtrude","SWEPT_EDGE",EDGE,{"disambiguationData":[OSD([sQuery(id+"F0.wireOp",EDGE,"E0.sketch_text.stroke-120"),sQuery(id+"F0.wireOp",EDGE,"E0.sketch_text.stroke-121")])]});
            var Q61;
            Q61=makeQuery(id+"F1.opExtrude","SWEPT_EDGE",EDGE,{"disambiguationData":[OSD([sQuery(id+"F0.wireOp",EDGE,"E0.sketch_text.stroke-119"),sQuery(id+"F0.wireOp",EDGE,"E0.sketch_text.stroke-120")])]});
            var Q62;
            Q62=makeQuery(id+"F1.opExtrude","SWEPT_EDGE",EDGE,{"disambiguationData":[OSD([sQuery(id+"F0.wireOp",EDGE,"E0.sketch_text.stroke-118"),sQuery(id+"F0.wireOp",EDGE,"E0.sketch_text.stroke-119")])]});
            var Q63;
            Q63=makeQuery(id+"F1.opExtrude","SWEPT_EDGE",EDGE,{"disambiguationData":[OSD([sQuery(id+"F0.wireOp",EDGE,"E0.sketch_text.stroke-117"),sQuery(id+"F0.wireOp",EDGE,"E0.sketch_text.stroke-118")])]});
            var Q64;
            Q64=makeQuery(id+"F1.opExtrude","SWEPT_EDGE",EDGE,{"disambiguationData":[OSD([sQuery(id+"F0.wireOp",EDGE,"E0.sketch_text.stroke-131"),sQuery(id+"F0.wireOp",EDGE,"E0.sketch_text.stroke-132")])]});
            var Q65;
            Q65=makeQuery(id+"F1.opExtrude","SWEPT_EDGE",EDGE,{"disambiguationData":[OSD([sQuery(id+"F0.wireOp",EDGE,"E0.sketch_text.stroke-137"),sQuery(id+"F0.wireOp",EDGE,"E0.sketch_text.stroke-138")])]});
            var Q66;
            Q66=makeQuery(id+"F1.opExtrude","SWEPT_EDGE",EDGE,{"disambiguationData":[OSD([sQuery(id+"F0.wireOp",EDGE,"E0.sketch_text.stroke-136"),sQuery(id+"F0.wireOp",EDGE,"E0.sketch_text.stroke-137")])]});
            var Q67;
            Q67=makeQuery(id+"F1.opExtrude","SWEPT_EDGE",EDGE,{"disambiguationData":[OSD([sQuery(id+"F0.wireOp",EDGE,"E0.sketch_text.stroke-138"),sQuery(id+"F0.wireOp",EDGE,"E0.sketch_text.stroke-139")])]});
            var Q68;
            Q68=makeQuery(id+"F1.opExtrude","SWEPT_EDGE",EDGE,{"disambiguationData":[OSD([sQuery(id+"F0.wireOp",EDGE,"E0.sketch_text.stroke-123"),sQuery(id+"F0.wireOp",EDGE,"E0.sketch_text.stroke-140")])]});
            var Q69;
            Q69=makeQuery(id+"F1.opExtrude","SWEPT_EDGE",EDGE,{"disambiguationData":[OSD([sQuery(id+"F0.wireOp",EDGE,"E0.sketch_text.stroke-123"),sQuery(id+"F0.wireOp",EDGE,"E0.sketch_text.stroke-124")])]});
            var Q70;
            Q70=makeQuery(id+"F1.opExtrude","SWEPT_EDGE",EDGE,{"disambiguationData":[OSD([sQuery(id+"F0.wireOp",EDGE,"E0.sketch_text.stroke-124"),sQuery(id+"F0.wireOp",EDGE,"E0.sketch_text.stroke-125")])]});
            fillet(context, id + "F2", {"entities" : qUnion([Q0, Q1, Q2, Q3, Q4, Q5, Q6, Q7, Q8, Q9, Q10, Q11, Q12, Q13, Q14, Q15, Q16, Q17, Q18, Q19, Q20, Q21, Q22, Q23, Q24, Q25, Q26, Q27, Q28, Q29, Q30, Q31, Q32, Q33, Q34, Q35, Q36, Q37, Q38, Q39, Q40, Q41, Q42, Q43, Q44, Q45, Q46, Q47, Q48, Q49, Q50, Q51, Q52, Q53, Q54, Q55, Q56, Q57, Q58, Q59, Q60, Q61, Q62, Q63, Q64, Q65, Q66, Q67, Q68, Q69, Q70]), "radius" : 1 * mm, "tangentPropagation" : true, "allowEdgeOverflow" : false});
        }
    });
